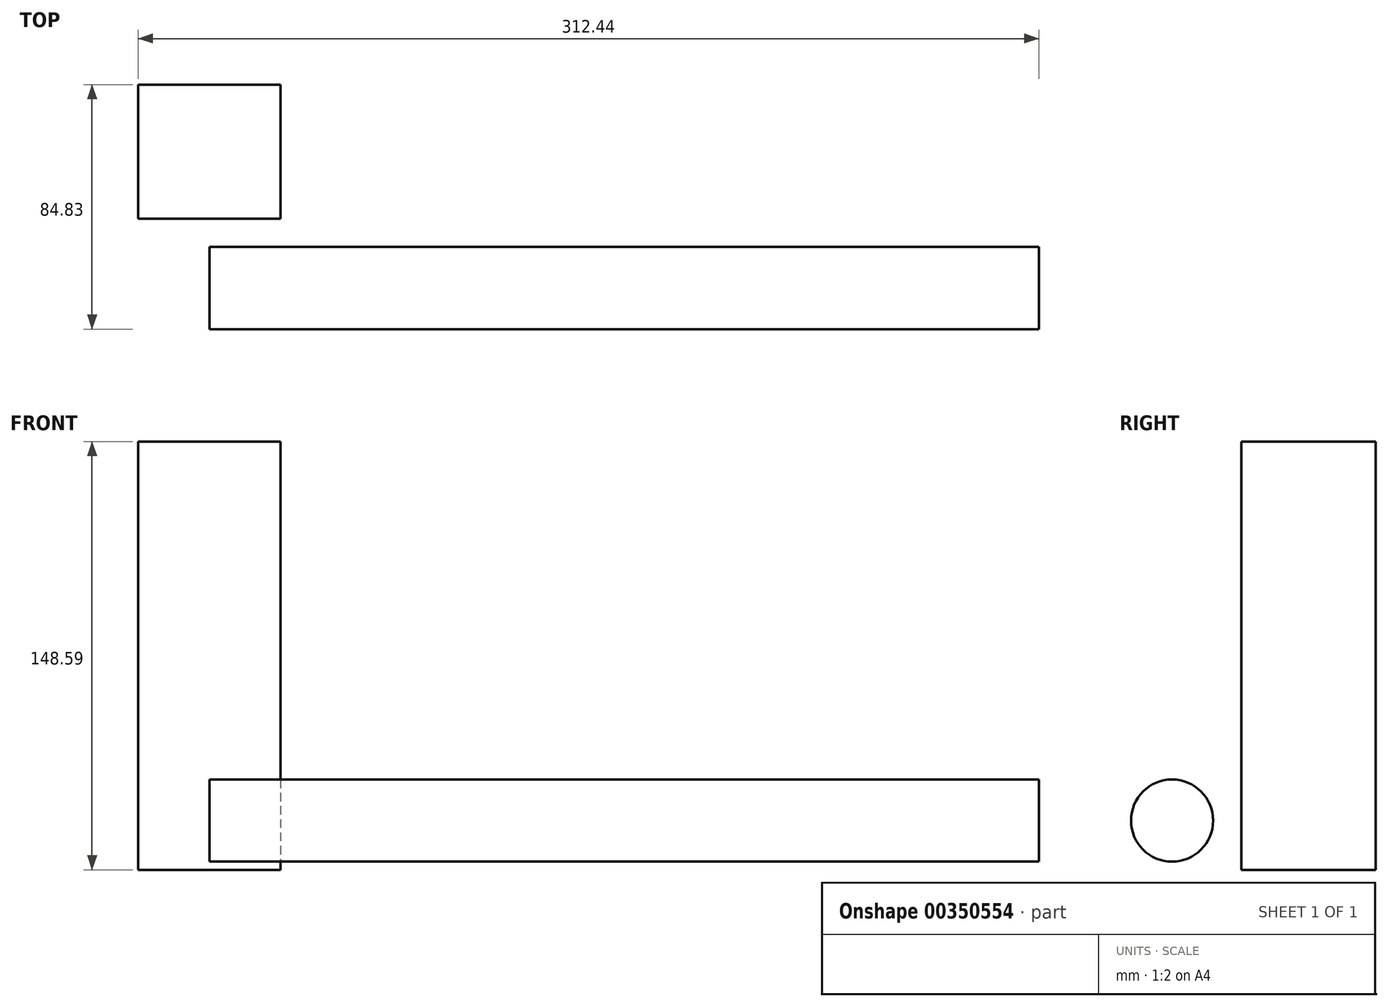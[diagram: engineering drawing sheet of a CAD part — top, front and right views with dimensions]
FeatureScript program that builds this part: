
annotation { "Feature Type Name" : "Feature", "Feature Type Description" : "" }
export const myFeature = defineFeature(function(context is Context, id is Id, definition is map)
    precondition{}
    {
        {
            var Q0;
            Q0=qCreatedBy(makeId("Top.planeOp"),FACE);
            var sketch = newSketch(context, id + "F0", { "sketchPlane" : qUnion([Q0])});
            skLineSegment(sketch, "E0.bottom", {"start": v(24.66, 23.26) * mm, "end": v(-24.66, 23.26) * mm});
            skLineSegment(sketch, "E0.top", {"start": v(24.66, -23.26) * mm, "end": v(-24.66, -23.26) * mm});
            skLineSegment(sketch, "E0.left", {"start": v(24.66, 23.26) * mm, "end": v(24.66, -23.26) * mm});
            skLineSegment(sketch, "E0.right", {"start": v(-24.66, 23.26) * mm, "end": v(-24.66, -23.26) * mm});
            skPoint(sketch, "E0.middle", {"position": v(0, 0) * mm});
            skSolve(sketch);
        }
        {
            var Q0;
            Q0 = qSketchRegion(id + "F0", true);
            extrude(context, id + "F1", {"entities" : qUnion([Q0]), "depth" : 148.6 * mm});
        }
        {
            var Q0;
            Q0=qCreatedBy(makeId("Right.planeOp"),FACE);
            var sketch = newSketch(context, id + "F2", { "sketchPlane" : qUnion([Q0])});
            skCircle(sketch, "E1", {"center": v(-47.32, 17.08) * mm, "radius": 14.25 * mm});
            skSolve(sketch);
        }
        {
            var Q0;
            Q0 = qSketchRegion(id + "F2", true);
            extrude(context, id + "F3", {"entities" : qUnion([Q0]), "depth" : 287.78 * mm});
        }
    });
